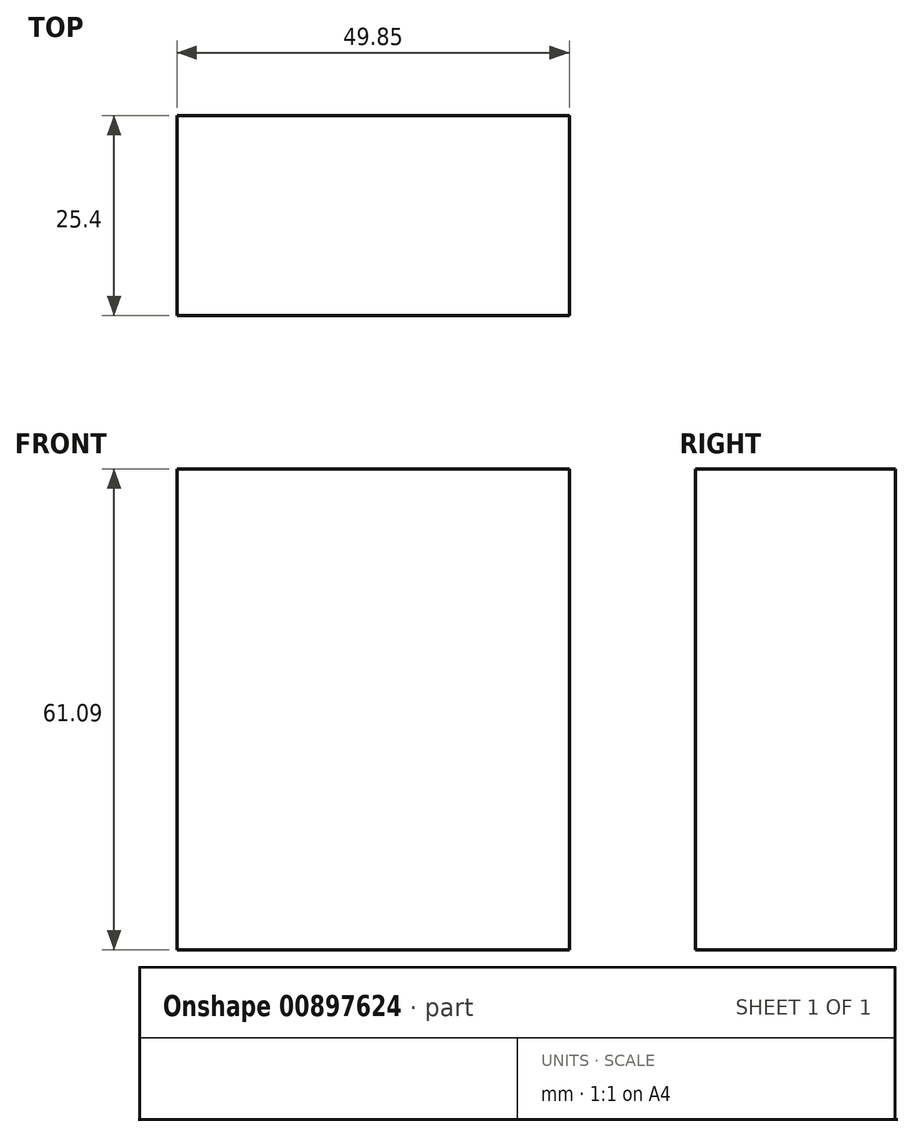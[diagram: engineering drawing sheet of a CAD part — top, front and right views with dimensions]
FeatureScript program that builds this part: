
annotation { "Feature Type Name" : "Feature", "Feature Type Description" : "" }
export const myFeature = defineFeature(function(context is Context, id is Id, definition is map)
    precondition{}
    {
        {
            var Q0;
            Q0=qCreatedBy(makeId("Front.planeOp"),FACE);
            var sketch = newSketch(context, id + "F0", { "sketchPlane" : qUnion([Q0])});
            skLineSegment(sketch, "E0.bottom", {"start": v(-24.05, 3.23) * mm, "end": v(25.8, 3.23) * mm});
            skLineSegment(sketch, "E0.top", {"start": v(-24.05, 64.32) * mm, "end": v(25.8, 64.32) * mm});
            skLineSegment(sketch, "E0.left", {"start": v(-24.05, 3.23) * mm, "end": v(-24.05, 64.32) * mm});
            skLineSegment(sketch, "E0.right", {"start": v(25.8, 3.23) * mm, "end": v(25.8, 64.32) * mm});
            skPoint(sketch, "E1.oppositeSnap0", {"position": v(76.68, 20.86) * mm});
            skPoint(sketch, "E2.orphan", {"position": v(76.68, 41.72) * mm});
            skPoint(sketch, "E1.right.end.orphan", {"position": v(53.68, 20.86) * mm});
            skPoint(sketch, "E3.bottom.end.orphan", {"position": v(76.68, 0) * mm});
            skPoint(sketch, "E4.right.end.orphan", {"position": v(19.87, 0) * mm});
            skLineSegment(sketch, "E5.left", {"start": v(-24.05, 64.32) * mm, "end": v(-24.05, 3.32) * mm});
            skSolve(sketch);
        }
        {
            var Q0;
            Q0 = qSketchRegion(id + "F0", true);
            extrude(context, id + "F1", {"entities" : qUnion([Q0]), "depth" : 25.4 * mm, "offsetDistance" : 25.4 * mm});
        }
    });
